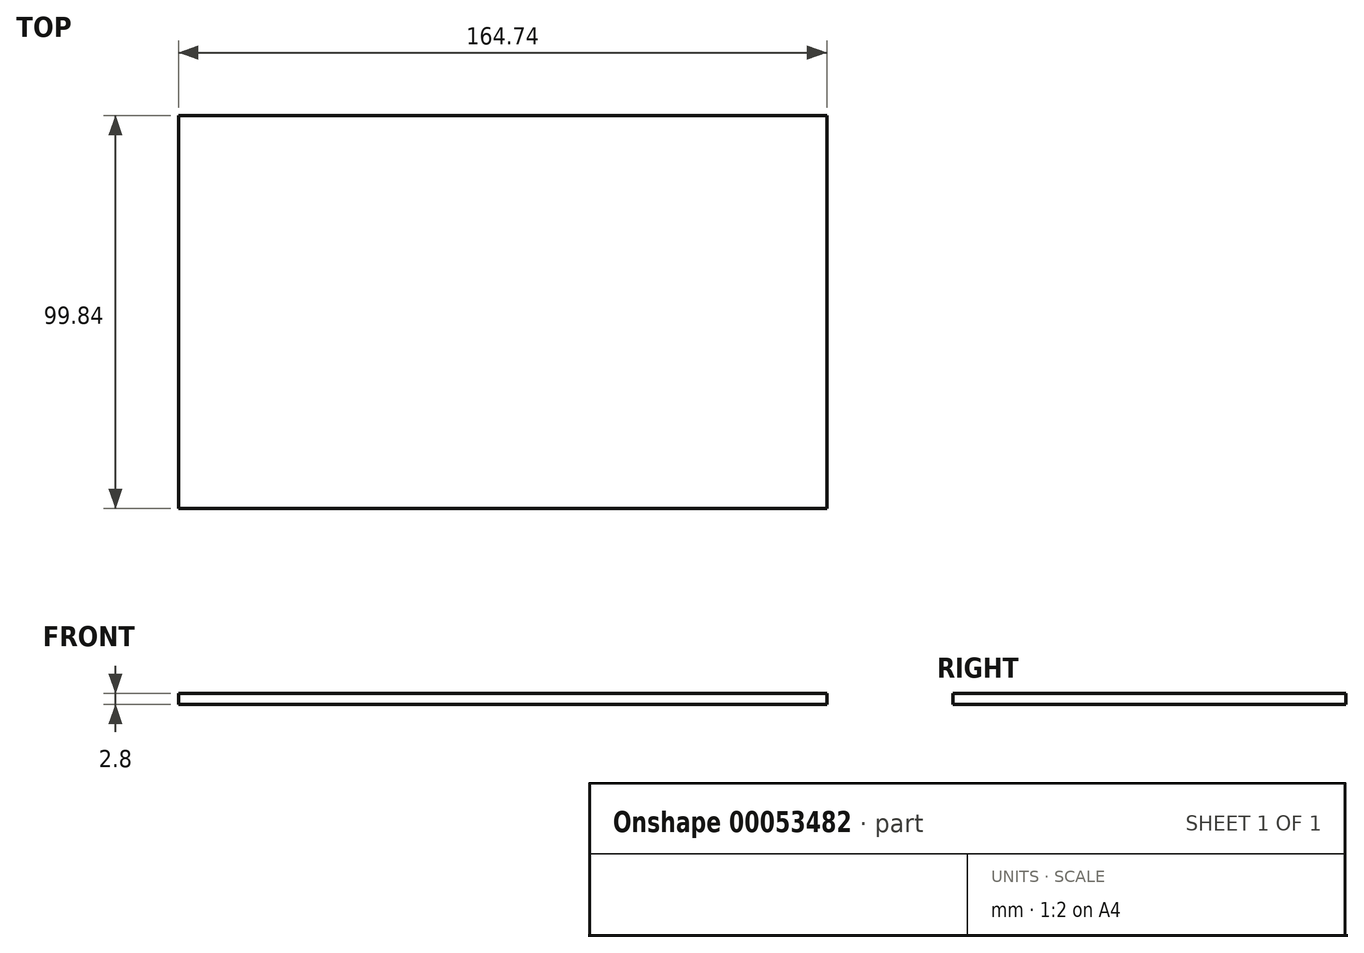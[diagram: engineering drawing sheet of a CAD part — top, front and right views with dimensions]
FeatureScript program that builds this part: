
annotation { "Feature Type Name" : "Feature", "Feature Type Description" : "" }
export const myFeature = defineFeature(function(context is Context, id is Id, definition is map)
    precondition{}
    {
        {
            var Q0;
            Q0=qCreatedBy(makeId("Top.planeOp"),FACE);
            var sketch = newSketch(context, id + "F0", { "sketchPlane" : qUnion([Q0])});
            skLineSegment(sketch, "E0.rect.bottom", {"start": v(-82.37, 49.92) * mm, "end": v(82.37, 49.92) * mm});
            skLineSegment(sketch, "E0.rect.top", {"start": v(-82.37, -49.92) * mm, "end": v(82.37, -49.92) * mm});
            skLineSegment(sketch, "E0.rect.left", {"start": v(-82.37, 49.92) * mm, "end": v(-82.37, -49.92) * mm});
            skLineSegment(sketch, "E0.rect.right", {"start": v(82.37, 49.92) * mm, "end": v(82.37, -49.92) * mm});
            skPoint(sketch, "E0.rect.middle", {"position": v(0, 0) * mm});
            skSolve(sketch);
        }
        {
            var Q0;
            Q0 = qSketchRegion(id + "F0", true);
            extrude(context, id + "F1", {"entities" : qUnion([Q0]), "depth" : 2.8 * mm});
        }
    });
